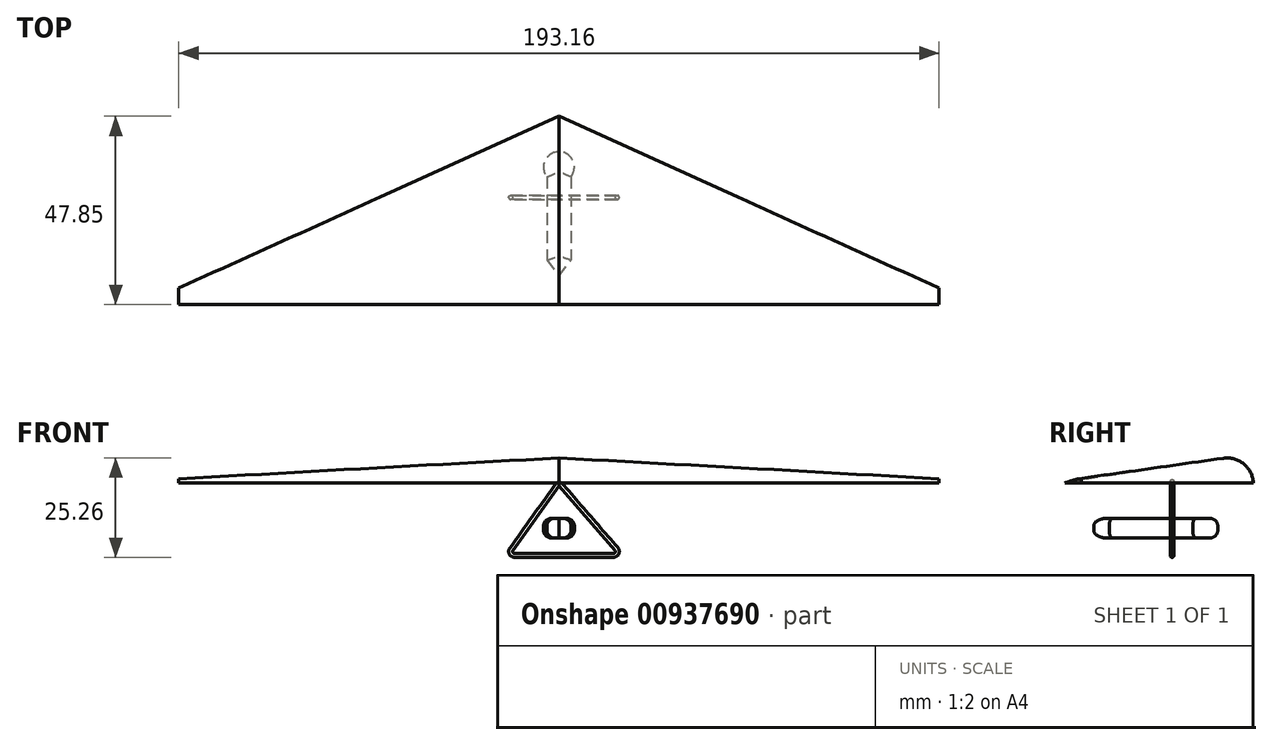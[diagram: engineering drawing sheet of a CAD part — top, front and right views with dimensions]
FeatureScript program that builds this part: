
annotation { "Feature Type Name" : "Feature", "Feature Type Description" : "" }
export const myFeature = defineFeature(function(context is Context, id is Id, definition is map)
    precondition{}
    {
        {
            var Q0;
            Q0=qCreatedBy(makeId("Top.planeOp"),FACE);
            var sketch = newSketch(context, id + "F0", { "sketchPlane" : qUnion([Q0])});
            skLineSegment(sketch, "E0", {"start": v(0, 43.73) * mm, "end": v(-96.58, 0) * mm});
            skLineSegment(sketch, "E1", {"start": v(-96.58, 0) * mm, "end": v(-96.58, -4.12) * mm});
            skLineSegment(sketch, "E2", {"start": v(-96.58, -4.12) * mm, "end": v(93.64, -4.12) * mm});
            skLineSegment(sketch, "E3", {"start": v(93.64, -4.12) * mm, "end": v(93.64, 0) * mm});
            skLineSegment(sketch, "E4", {"start": v(93.64, 0) * mm, "end": v(0, 43.73) * mm});
            skSolve(sketch);
        }
        {
            var Q0;
            Q0=qCreatedBy(makeId("Right.planeOp"),FACE);
            var sketch = newSketch(context, id + "F1", { "sketchPlane" : qUnion([Q0])});
            skArc(sketch, "E5", {"start": v(43.73, 0) * mm, "mid": v(41.25, 4.8) * mm, "end": v(36.02, 6.21) * mm});
            skLineSegment(sketch, "E6", {"start": v(36.02, 6.21) * mm, "end": v(-4.12, 0) * mm});
            skLineSegment(sketch, "E7", {"start": v(43.73, 0) * mm, "end": v(-4.12, 0) * mm});
            skSolve(sketch);
        }
        {
            var Q0;
            Q0=sQuery(id+"F0.wireOp",EDGE,"E1");
            var Q1;
            Q1=qCreatedBy(makeId("Right.planeOp"),FACE);
            cPlane(context, id + "F2", {"entities" : qUnion([Q0, Q1]), "cplaneType" : CPlaneType.LINE_ANGLE, "offset" : 25 * mm, "angle" : 0 * degree, "width" : 150 * mm, "height" : 150 * mm});
        }
        {
            var Q0;
            Q0=qCreatedBy(id+"F2.planeOp",FACE);
            var sketch = newSketch(context, id + "F3", { "sketchPlane" : qUnion([Q0])});
            skArc(sketch, "E8", {"start": v(0.82, 1) * mm, "mid": v(0.08, 0.77) * mm, "end": v(0, 0) * mm});
            skLineSegment(sketch, "E9", {"start": v(0.82, 1) * mm, "end": v(4.12, 0) * mm});
            skLineSegment(sketch, "E10", {"start": v(0, 0) * mm, "end": v(4.12, 0) * mm});
            skSolve(sketch);
        }
        {
            var Q0;
            Q0=qSketchRegion(id+"F1",true);
            var Q1;
            Q1=qSketchRegion(id+"F3",true);
            var Q2;
            Q2=sQuery(id+"F0.wireOp",EDGE,"E0");
            loft(context, id + "F4", {"addGuides" : true, "sheetProfilesArray" : [{ "sheetProfileEntities" : qUnion([Q0]) }, { "sheetProfileEntities" : qUnion([Q1]) }], "guidesArray" : [{ "guideEntities" : qUnion([Q2]), "guideDerivativeType" : LoftGuideDerivativeType.DEFAULT, "guideDerivativeMagnitude" : 1 }]});
        }
        {
            var Q0;
            Q0=makeQuery(id+"F4.opLoft","SWEPT_BODY",BODY,{"disambiguationData":[OSD([sQuery(id+"F0.wireOp",EDGE,"E0"),makeQuery(id+"F1.imprint","IMPRINT",FACE,{"disambiguationData":[TD([[makeQuery(id+"F1.imprint","IMPRINT",EDGE,{"derivedFrom":sQuery(id+"F1.wireOp",EDGE,"E5")}),1.0]])]}),makeQuery(id+"F3.imprint","IMPRINT",FACE,{"disambiguationData":[TD([[makeQuery(id+"F3.imprint","IMPRINT",EDGE,{"derivedFrom":sQuery(id+"F3.wireOp",EDGE,"E8")}),1.0]])]})])]});
            var Q1;
            Q1=qCreatedBy(makeId("Right.planeOp"),FACE);
            mirror(context, id + "F5", {"operationType" : NewBodyOperationType.ADD, "entities" : qUnion([Q0]), "mirrorPlane" : qUnion([Q1])});
        }
        {
            var Q0;
            Q0=qCreatedBy(makeId("Right.planeOp"),FACE);
            var sketch = newSketch(context, id + "F6", { "sketchPlane" : qUnion([Q0])});
            skLineSegment(sketch, "E11", {"start": v(23.08, 0) * mm, "end": v(23.08, -11.55) * mm});
            skSolve(sketch);
        }
        {
            var Q0;
            Q0=sQuery(id+"F6.wireOp",EDGE,"E11");
            var Q1;
            Q1=qCreatedBy(makeId("Right.planeOp"),FACE);
            cPlane(context, id + "F7", {"entities" : qUnion([Q0, Q1]), "cplaneType" : CPlaneType.LINE_ANGLE, "offset" : 25 * mm, "angle" : 90 * degree, "width" : 150 * mm, "height" : 150 * mm});
        }
        {
            var Q0;
            Q0=qCreatedBy(id+"F7.planeOp",FACE);
            var sketch = newSketch(context, id + "F8", { "sketchPlane" : qUnion([Q0])});
            skLineSegment(sketch, "E12", {"start": v(0, 0) * mm, "end": v(12.09, -16.89) * mm});
            skLineSegment(sketch, "E13", {"start": v(11.27, -18.47) * mm, "end": v(-13.84, -18.47) * mm});
            skLineSegment(sketch, "E14", {"start": v(-14.6, -16.81) * mm, "end": v(0, 0) * mm});
            skPoint(sketch, "E15.visualSharp", {"position": v(13.22, -18.47) * mm});
            skArc(sketch, "E15.filletArc", {"start": v(11.27, -18.47) * mm, "mid": v(12.16, -17.93) * mm, "end": v(12.09, -16.89) * mm});
            skPoint(sketch, "E16.visualSharp", {"position": v(-16.03, -18.47) * mm});
            skArc(sketch, "E16.filletArc", {"start": v(-14.6, -16.81) * mm, "mid": v(-14.74, -17.88) * mm, "end": v(-13.84, -18.47) * mm});
            skSolve(sketch);
        }
        {
            var Q0;
            Q0=qCreatedBy(makeId("Right.planeOp"),FACE);
            var sketch = newSketch(context, id + "F9", { "sketchPlane" : qUnion([Q0])});
            skCircle(sketch, "E17", {"center": v(23.08, -18.47) * mm, "radius": 0.5 * mm});
            skSolve(sketch);
        }
        {
            var Q0;
            Q0=qSketchRegion(id+"F9",true);
            var Q1;
            Q1=qConstructionFilter(qBodyType(qCreatedBy(id+"F8",EDGE),BodyType.WIRE),ConstructionObject.NO);
            sweep(context, id + "F10", {"profiles" : qUnion([Q0]), "path" : qUnion([Q1])});
        }
        {
            var Q0;
            Q0=qCreatedBy(id+"F7.planeOp",FACE);
            var sketch = newSketch(context, id + "F11", { "sketchPlane" : qUnion([Q0])});
            skLineSegment(sketch, "E18", {"start": v(0, -11.55) * mm, "end": v(-15.8, -11.55) * mm});
            skSolve(sketch);
        }
        {
            var Q0;
            Q0=sQuery(id+"F11.wireOp",EDGE,"E18");
            cPlane(context, id + "F12", {"entities" : qUnion([Q0]), "cplaneType" : CPlaneType.LINE_ANGLE, "offset" : 25 * mm, "angle" : 90 * degree, "width" : 150 * mm, "height" : 150 * mm});
        }
        {
            var Q0;
            Q0=qCreatedBy(id+"F12.planeOp",FACE);
            var sketch = newSketch(context, id + "F13", { "sketchPlane" : qUnion([Q0])});
            skCircle(sketch, "E19", {"center": v(0, 30.76) * mm, "radius": 3.92 * mm});
            skLineSegment(sketch, "E20.bottom", {"start": v(-3.05, 28.3) * mm, "end": v(3.05, 28.3) * mm});
            skLineSegment(sketch, "E20.top", {"start": v(-3.05, 7.12) * mm, "end": v(3.05, 7.12) * mm});
            skLineSegment(sketch, "E20.left", {"start": v(-3.05, 28.3) * mm, "end": v(-3.05, 7.12) * mm});
            skLineSegment(sketch, "E20.right", {"start": v(3.05, 28.3) * mm, "end": v(3.05, 7.12) * mm});
            skLineSegment(sketch, "E21", {"start": v(-3.05, 7.12) * mm, "end": v(0, 3.17) * mm});
            skPoint(sketch, "E21.endSnap0", {"position": v(0, 7.12) * mm});
            skLineSegment(sketch, "E22", {"start": v(0, 3.17) * mm, "end": v(3.05, 7.12) * mm});
            skSolve(sketch);
        }
        {
            var Q0;
            Q0=qSketchRegion(id+"F13",true);
            extrude(context, id + "F14", {"entities" : qUnion([Q0]), "endBound" : BoundingType.SYMMETRIC, "depth" : 5 * mm, "offsetDistance" : 25 * mm});
        }
        {
            var Q0;
            Q0=makeQuery(id+"F14.opExtrude","CAP_EDGE",EDGE,{"disambiguationData":[OSD([sQuery(id+"F13.wireOp",EDGE,"E19")])],"isStart":false});
            var Q1;
            Q1=makeQuery(id+"F14.opExtrude","CAP_EDGE",EDGE,{"disambiguationData":[OSD([sQuery(id+"F13.wireOp",EDGE,"E19")])],"isStart":true});
            var Q2;
            Q2=makeQuery(id+"F14.opExtrude","CAP_EDGE",EDGE,{"disambiguationData":[OSD([sQuery(id+"F13.wireOp",EDGE,"E20.left")])],"isStart":true});
            var Q3;
            Q3=makeQuery(id+"F14.opExtrude","CAP_EDGE",EDGE,{"disambiguationData":[OSD([sQuery(id+"F13.wireOp",EDGE,"E20.left")])],"isStart":false});
            var Q4;
            Q4=makeQuery(id+"F14.opExtrude","CAP_EDGE",EDGE,{"disambiguationData":[OSD([sQuery(id+"F13.wireOp",EDGE,"E20.right")])],"isStart":false});
            var Q5;
            Q5=makeQuery(id+"F14.opExtrude","CAP_EDGE",EDGE,{"disambiguationData":[OSD([sQuery(id+"F13.wireOp",EDGE,"E20.right")])],"isStart":true});
            var Q6;
            Q6=makeQuery(id+"F14.opExtrude","CAP_EDGE",EDGE,{"disambiguationData":[OSD([sQuery(id+"F13.wireOp",EDGE,"E22")])],"isStart":true});
            var Q7;
            Q7=makeQuery(id+"F14.opExtrude","CAP_EDGE",EDGE,{"disambiguationData":[OSD([sQuery(id+"F13.wireOp",EDGE,"E21")])],"isStart":true});
            var Q8;
            Q8=makeQuery(id+"F14.opExtrude","CAP_EDGE",EDGE,{"disambiguationData":[OSD([sQuery(id+"F13.wireOp",EDGE,"E21")])],"isStart":false});
            var Q9;
            Q9=makeQuery(id+"F14.opExtrude","CAP_EDGE",EDGE,{"disambiguationData":[OSD([sQuery(id+"F13.wireOp",EDGE,"E22")])],"isStart":false});
            fillet(context, id + "F15", {"entities" : qUnion([Q0, Q1, Q2, Q3, Q4, Q5, Q6, Q7, Q8, Q9]), "radius" : 2 * mm, "tangentPropagation" : true, "allowEdgeOverflow" : false});
        }
    });
